# Revit family: LEPC14
name_source: partatom
category: Lighting Fixtures
revit_build: Autodesk Revit MEP 2012 (Build: 20110916_2132(x64)
units: mm (PartAtom-declared; Revit-internal decimal feet)

## types (1)
- LEPC14-40VL-LL
    Apparent Load = 0 VA
    Backbox = White
    Color Filter = 16777215
    Default Elevation = 4.00'
    Description = A e•poc® LED full distribution luminaire, with advanced solid state electronics, has significantly improved performance to offer additional lumen packages for maximum versatility.
    Dimming Lamp Color Temperature Shift = <None>
    Emit from Line Length = 2.00'
    Glass = White Glass
    Lamp = LED LAMP
    Lumens Output = Very High Lumen
    Manufacturer = Columbia Lighting
    Manufacturer Fax = (866)-898-1065
    Model = LEPC14
    Nominal Watts = 62 W
    Photometric Web File = LEPC14-40VL-LL.ies
    Product Documentation Link = http://www.columbialighting.com
    Product Page URL = http://www.columbialighting.com
    Row Length = 4.00'
    Shielding = Low Lamp Image
    Tilt Angle = -90.00°
    URL = http://www.columbialighting.com
    Voltage = 120 V

## geometry (parser evidence)
native form markers: Sweep x4
no freeform markers — native parametric forms only
